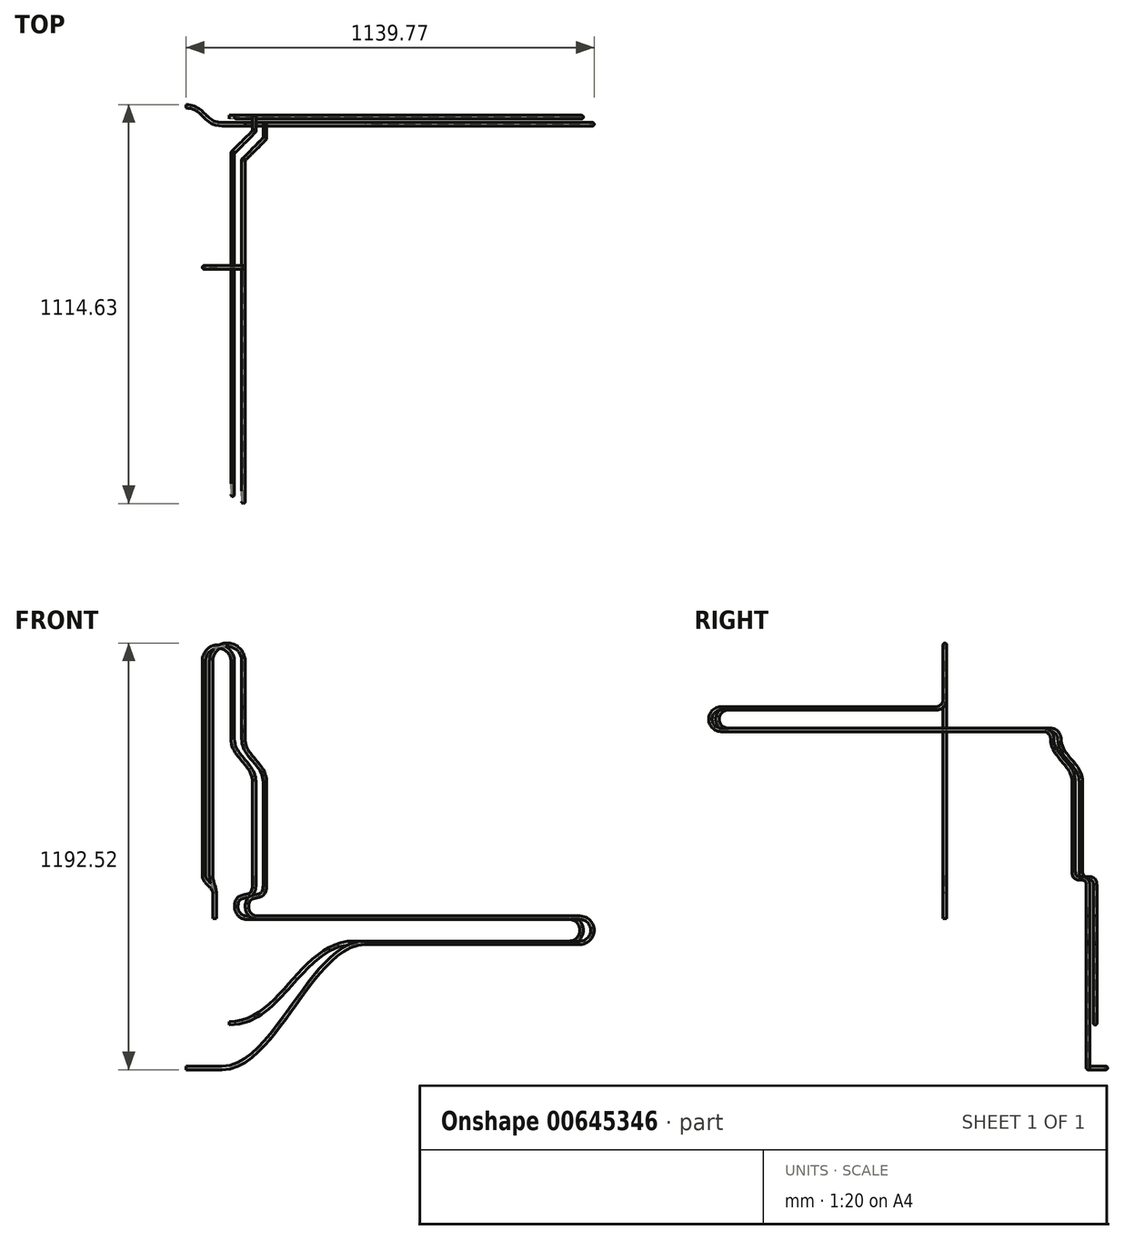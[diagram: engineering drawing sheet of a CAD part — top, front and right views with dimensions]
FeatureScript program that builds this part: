
annotation { "Feature Type Name" : "Feature", "Feature Type Description" : "" }
export const myFeature = defineFeature(function(context is Context, id is Id, definition is map)
    precondition{}
    {
        {
            var Q0;
            Q0=qCreatedBy(makeId("Top.planeOp"),FACE);
            var sketch = newSketch(context, id + "F0", { "sketchPlane" : qUnion([Q0])});
            skCircle(sketch, "E0", {"center": v(0, 0) * mm, "radius": 4.76 * mm});
            skCircle(sketch, "E1", {"center": v(0, 0) * mm, "radius": 3.17 * mm});
            skSolve(sketch);
        }
        {
            var Q0;
            Q0=qCreatedBy(makeId("Front.planeOp"),FACE);
            var sketch = newSketch(context, id + "F1", { "sketchPlane" : qUnion([Q0])});
            skLineSegment(sketch, "E2", {"start": v(80, 612) * mm, "end": v(80, 720) * mm});
            skArc(sketch, "E3", {"start": v(80, 720) * mm, "mid": v(35, 765) * mm, "end": v(-10, 720) * mm});
            skLineSegment(sketch, "E4", {"start": v(0, 70) * mm, "end": v(0, 0) * mm});
            skFitSpline(sketch, "E5", {"points": [v(0, 70) * mm, v(-5, 95) * mm, v(-10, 120) * mm], "startDerivative": vector(0, 60) * mm, "endDerivative": vector(0, 60) * mm});
            skLineSegment(sketch, "E6", {"start": v(-10, 110) * mm, "end": v(-10, 120) * mm, "construction": true});
            skLineSegment(sketch, "E7", {"start": v(0, 80) * mm, "end": v(0, 70) * mm, "construction": true});
            skLineSegment(sketch, "E8", {"start": v(0, 70) * mm, "end": v(-10, 120) * mm, "construction": true});
            skLineSegment(sketch, "E9", {"start": v(-10, 120) * mm, "end": v(-10, 720) * mm});
            skSolve(sketch);
        }
        {
            var Q0;
            Q0=qCreatedBy(makeId("Right.planeOp"),FACE);
            var Q1;
            Q1=sQuery(id+"F1.wireOp",VERTEX,"E2.start");
            cPlane(context, id + "F2", {"entities" : qUnion([Q0, Q1]), "cplaneType" : CPlaneType.PLANE_POINT, "offset" : 25 * mm, "width" : 150 * mm, "height" : 150 * mm});
        }
        {
            var Q0;
            Q0=qCreatedBy(id+"F2.planeOp",FACE);
            var sketch = newSketch(context, id + "F3", { "sketchPlane" : qUnion([Q0])});
            skArc(sketch, "E10.MirrorCS", {"start": v(0, 612) * mm, "mid": v(-7.32, 594.32) * mm, "end": v(-25, 587) * mm});
            skArc(sketch, "E11.MirrorCS", {"start": v(275, 527) * mm, "mid": v(292.68, 519.68) * mm, "end": v(300, 502) * mm});
            skLineSegment(sketch, "E12.MirrorCS", {"start": v(300, 502) * mm, "end": v(300, 517.1) * mm, "construction": true});
            skLineSegment(sketch, "E13.MirrorCS", {"start": v(-25, 587) * mm, "end": v(-625, 587) * mm});
            skArc(sketch, "E14.MirrorCS", {"start": v(-625, 527) * mm, "mid": v(-655, 557) * mm, "end": v(-625, 587) * mm});
            skLineSegment(sketch, "E15.MirrorCS", {"start": v(-625, 527) * mm, "end": v(275, 527) * mm});
            skSolve(sketch);
        }
        {
            var Q0;
            Q0=sQuery(id+"F3.wireOp",EDGE,"E12.MirrorCS");
            cPlane(context, id + "F4", {"entities" : qUnion([Q0]), "cplaneType" : CPlaneType.LINE_ANGLE, "offset" : 25 * mm, "angle" : 45 * degree, "oppositeDirection" : true, "width" : 150 * mm, "height" : 150 * mm});
        }
        {
            var Q0;
            Q0=qCreatedBy(id+"F4.planeOp",FACE);
            var sketch = newSketch(context, id + "F5", { "sketchPlane" : qUnion([Q0])});
            skFitSpline(sketch, "E16", {"points": [v(268.7, 502) * mm, v(311.2, 442) * mm, v(353.7, 382) * mm], "startDerivative": vector(0, -150) * mm, "endDerivative": vector(0, -150) * mm});
            skLineSegment(sketch, "E17", {"start": v(268.7, 477) * mm, "end": v(268.7, 502) * mm, "construction": true});
            skLineSegment(sketch, "E18", {"start": v(353.7, 407) * mm, "end": v(353.7, 382) * mm, "construction": true});
            skLineSegment(sketch, "E19", {"start": v(353.7, 382) * mm, "end": v(268.7, 502) * mm, "construction": true});
            skLineSegment(sketch, "E20", {"start": v(353.7, 382) * mm, "end": v(353.7, 132) * mm});
            skSolve(sketch);
        }
        {
            var Q0;
            Q0=qCreatedBy(makeId("Right.planeOp"),FACE);
            var Q1;
            Q1=sQuery(id+"F5.wireOp",VERTEX,"E20.end");
            cPlane(context, id + "F6", {"entities" : qUnion([Q0, Q1]), "cplaneType" : CPlaneType.PLANE_POINT, "offset" : 25 * mm, "width" : 150 * mm, "height" : 150 * mm});
        }
        {
            var Q0;
            Q0=qCreatedBy(id+"F6.planeOp",FACE);
            var sketch = newSketch(context, id + "F7", { "sketchPlane" : qUnion([Q0])});
            skFitSpline(sketch, "E21", {"points": [v(360.1, 132) * mm, v(380.1, 112) * mm, v(400.1, 92) * mm], "startDerivative": vector(0, -120) * mm, "endDerivative": vector(0, -120) * mm});
            skLineSegment(sketch, "E22", {"start": v(360.1, 132) * mm, "end": v(360.1, 112) * mm, "construction": true});
            skLineSegment(sketch, "E23", {"start": v(400.1, 112) * mm, "end": v(400.1, 92) * mm, "construction": true});
            skLineSegment(sketch, "E24", {"start": v(400.1, 92) * mm, "end": v(360.1, 132) * mm, "construction": true});
            skSolve(sketch);
        }
        {
            var Q0;
            Q0=sQuery(id+"F7.wireOp",VERTEX,"E21.end");
            var Q1;
            Q1=qCreatedBy(makeId("Front.planeOp"),FACE);
            cPlane(context, id + "F8", {"entities" : qUnion([Q0, Q1]), "cplaneType" : CPlaneType.PLANE_POINT, "offset" : 25 * mm, "width" : 150 * mm, "height" : 150 * mm});
        }
        {
            var Q0;
            Q0=qCreatedBy(id+"F8.planeOp",FACE);
            var sketch = newSketch(context, id + "F9", { "sketchPlane" : qUnion([Q0])});
            skFitSpline(sketch, "E25", {"points": [v(140.1, 92) * mm, v(115.1, 62) * mm, v(90.1, 32) * mm], "startDerivative": vector(0, -150) * mm, "endDerivative": vector(0, -150) * mm});
            skLineSegment(sketch, "E26", {"start": v(140.1, 92) * mm, "end": v(140.1, 67) * mm, "construction": true});
            skLineSegment(sketch, "E27", {"start": v(90.1, 57) * mm, "end": v(90.1, 32) * mm, "construction": true});
            skLineSegment(sketch, "E28", {"start": v(90.1, 32) * mm, "end": v(140.1, 92) * mm, "construction": true});
            skArc(sketch, "E29", {"start": v(90.1, 32) * mm, "mid": v(98.9, 10.79) * mm, "end": v(120.1, 2) * mm});
            skLineSegment(sketch, "E30", {"start": v(120.1, 2) * mm, "end": v(1020.1, 2) * mm});
            skArc(sketch, "E31", {"start": v(1020.1, -68) * mm, "mid": v(1055.1, -33) * mm, "end": v(1020.1, 2) * mm});
            skLineSegment(sketch, "E32", {"start": v(1020.1, -68) * mm, "end": v(420.1, -68) * mm});
            skFitSpline(sketch, "E33", {"points": [v(420.1, -68) * mm, v(220.1, -243) * mm, v(20.1, -418) * mm], "startDerivative": vector(-450, 0) * mm, "endDerivative": vector(-450, 0) * mm});
            skLineSegment(sketch, "E34", {"start": v(420.1, -68) * mm, "end": v(345.1, -68) * mm, "construction": true});
            skLineSegment(sketch, "E35", {"start": v(95.1, -418) * mm, "end": v(20.1, -418) * mm, "construction": true});
            skLineSegment(sketch, "E36", {"start": v(20.1, -418) * mm, "end": v(420.1, -68) * mm, "construction": true});
            skSolve(sketch);
        }
        {
            var Q0;
            Q0=sQuery(id+"F9.wireOp",VERTEX,"E33.end");
            var Q1;
            Q1=qCreatedBy(makeId("Top.planeOp"),FACE);
            cPlane(context, id + "F10", {"entities" : qUnion([Q0, Q1]), "cplaneType" : CPlaneType.PLANE_POINT, "offset" : 25 * mm, "width" : 150 * mm, "height" : 150 * mm});
        }
        {
            var Q0;
            Q0=qCreatedBy(id+"F10.planeOp",FACE);
            var sketch = newSketch(context, id + "F11", { "sketchPlane" : qUnion([Q0])});
            skFitSpline(sketch, "E37", {"points": [v(20.1, 400.1) * mm, v(-29.9, 425.1) * mm, v(-79.9, 450.1) * mm], "startDerivative": vector(-150, 0) * mm, "endDerivative": vector(-150, 0) * mm});
            skLineSegment(sketch, "E38", {"start": v(-4.9, 400.1) * mm, "end": v(20.1, 400.1) * mm, "construction": true});
            skLineSegment(sketch, "E39", {"start": v(-54.9, 450.1) * mm, "end": v(-79.9, 450.1) * mm, "construction": true});
            skLineSegment(sketch, "E40", {"start": v(-79.9, 450.1) * mm, "end": v(20.1, 400.1) * mm, "construction": true});
            skSolve(sketch);
        }
        {
            var Q0;
            Q0=qSketchRegion(id+"F0",true);
            var Q1;
            Q1=qConstructionFilter(qBodyType(qCreatedBy(id+"F1",EDGE),BodyType.WIRE),ConstructionObject.NO);
            var Q2;
            Q2=qConstructionFilter(qBodyType(qCreatedBy(id+"F3",EDGE),BodyType.WIRE),ConstructionObject.NO);
            var Q3;
            Q3=qConstructionFilter(qBodyType(qCreatedBy(id+"F5",EDGE),BodyType.WIRE),ConstructionObject.NO);
            var Q4;
            Q4=qConstructionFilter(qBodyType(qCreatedBy(id+"F7",EDGE),BodyType.WIRE),ConstructionObject.NO);
            var Q5;
            Q5=qConstructionFilter(qBodyType(qCreatedBy(id+"F9",EDGE),BodyType.WIRE),ConstructionObject.NO);
            var Q6;
            Q6=qConstructionFilter(qBodyType(qCreatedBy(id+"F11",EDGE),BodyType.WIRE),ConstructionObject.NO);
            sweep(context, id + "F12", {"profiles" : qUnion([Q0]), "path" : qUnion([Q1, Q2, Q3, Q4, Q5, Q6])});
        }
        {
            var Q0;
            Q0=qCreatedBy(makeId("Front.planeOp"),FACE);
            var sketch = newSketch(context, id + "F13", { "sketchPlane" : qUnion([Q0])});
            skLineSegment(sketch, "E41", {"start": v(50, 612) * mm, "end": v(50, 720) * mm});
            skArc(sketch, "E42", {"start": v(50, 720) * mm, "mid": v(10, 760) * mm, "end": v(-30, 720) * mm});
            skLineSegment(sketch, "E43", {"start": v(0, 70) * mm, "end": v(0, 0) * mm});
            skFitSpline(sketch, "E44", {"points": [v(0, 70) * mm, v(-15, 95) * mm, v(-30, 120) * mm], "startDerivative": vector(0, 60) * mm, "endDerivative": vector(0, 60) * mm});
            skLineSegment(sketch, "E45", {"start": v(-30, 110) * mm, "end": v(-30, 120) * mm, "construction": true});
            skLineSegment(sketch, "E46", {"start": v(0, 80) * mm, "end": v(0, 70) * mm, "construction": true});
            skLineSegment(sketch, "E47", {"start": v(0, 70) * mm, "end": v(-30, 120) * mm, "construction": true});
            skLineSegment(sketch, "E48", {"start": v(-30, 120) * mm, "end": v(-30, 720) * mm});
            skSolve(sketch);
        }
        {
            var Q0;
            Q0=qCreatedBy(makeId("Right.planeOp"),FACE);
            var Q1;
            Q1=sQuery(id+"F13.wireOp",VERTEX,"E41.start");
            cPlane(context, id + "F14", {"entities" : qUnion([Q0, Q1]), "cplaneType" : CPlaneType.PLANE_POINT, "offset" : 25 * mm, "width" : 150 * mm, "height" : 150 * mm});
        }
        {
            var Q0;
            Q0=qCreatedBy(id+"F14.planeOp",FACE);
            var sketch = newSketch(context, id + "F15", { "sketchPlane" : qUnion([Q0])});
            skArc(sketch, "E49.MirrorCS", {"start": v(0, 612) * mm, "mid": v(-7.32, 594.32) * mm, "end": v(-25, 587) * mm});
            skArc(sketch, "E50.MirrorCS", {"start": v(295, 527) * mm, "mid": v(312.68, 519.68) * mm, "end": v(320, 502) * mm});
            skLineSegment(sketch, "E51.MirrorCS", {"start": v(320, 502) * mm, "end": v(320, 517.1) * mm, "construction": true});
            skLineSegment(sketch, "E52.MirrorCS", {"start": v(-25, 587) * mm, "end": v(-605, 587) * mm});
            skArc(sketch, "E53.MirrorCS", {"start": v(-605, 527) * mm, "mid": v(-635, 557) * mm, "end": v(-605, 587) * mm});
            skLineSegment(sketch, "E54.MirrorCS", {"start": v(-605, 527) * mm, "end": v(295, 527) * mm});
            skSolve(sketch);
        }
        {
            var Q0;
            Q0=sQuery(id+"F15.wireOp",EDGE,"E51.MirrorCS");
            cPlane(context, id + "F16", {"entities" : qUnion([Q0]), "cplaneType" : CPlaneType.LINE_ANGLE, "offset" : 25 * mm, "angle" : 45 * degree, "oppositeDirection" : true, "width" : 150 * mm, "height" : 150 * mm});
        }
        {
            var Q0;
            Q0=qCreatedBy(id+"F16.planeOp",FACE);
            var sketch = newSketch(context, id + "F17", { "sketchPlane" : qUnion([Q0])});
            skFitSpline(sketch, "E55", {"points": [v(261.63, 502) * mm, v(304.13, 442) * mm, v(346.63, 382) * mm], "startDerivative": vector(0, -150) * mm, "endDerivative": vector(0, -150) * mm});
            skLineSegment(sketch, "E56", {"start": v(261.63, 477) * mm, "end": v(261.63, 502) * mm, "construction": true});
            skLineSegment(sketch, "E57", {"start": v(346.63, 407) * mm, "end": v(346.63, 382) * mm, "construction": true});
            skLineSegment(sketch, "E58", {"start": v(346.63, 382) * mm, "end": v(261.63, 502) * mm, "construction": true});
            skLineSegment(sketch, "E59", {"start": v(346.63, 382) * mm, "end": v(346.63, 132) * mm});
            skSolve(sketch);
        }
        {
            var Q0;
            Q0=qCreatedBy(makeId("Right.planeOp"),FACE);
            var Q1;
            Q1=sQuery(id+"F17.wireOp",VERTEX,"E59.end");
            cPlane(context, id + "F18", {"entities" : qUnion([Q0, Q1]), "cplaneType" : CPlaneType.PLANE_POINT, "offset" : 25 * mm, "width" : 150 * mm, "height" : 150 * mm});
        }
        {
            var Q0;
            Q0=qCreatedBy(id+"F18.planeOp",FACE);
            var sketch = newSketch(context, id + "F19", { "sketchPlane" : qUnion([Q0])});
            skFitSpline(sketch, "E60", {"points": [v(380.1, 132) * mm, v(400.1, 112) * mm, v(420.1, 92) * mm], "startDerivative": vector(0, -120) * mm, "endDerivative": vector(0, -120) * mm});
            skLineSegment(sketch, "E61", {"start": v(380.1, 132) * mm, "end": v(380.1, 112) * mm, "construction": true});
            skLineSegment(sketch, "E62", {"start": v(420.1, 112) * mm, "end": v(420.1, 92) * mm, "construction": true});
            skLineSegment(sketch, "E63", {"start": v(420.1, 92) * mm, "end": v(380.1, 132) * mm, "construction": true});
            skSolve(sketch);
        }
        {
            var Q0;
            Q0=qCreatedBy(makeId("Front.planeOp"),FACE);
            var Q1;
            Q1=sQuery(id+"F19.wireOp",VERTEX,"E60.end");
            cPlane(context, id + "F20", {"entities" : qUnion([Q0, Q1]), "cplaneType" : CPlaneType.PLANE_POINT, "offset" : 25 * mm, "width" : 150 * mm, "height" : 150 * mm});
        }
        {
            var Q0;
            Q0=qCreatedBy(id+"F20.planeOp",FACE);
            var sketch = newSketch(context, id + "F21", { "sketchPlane" : qUnion([Q0])});
            skFitSpline(sketch, "E64", {"points": [v(110.1, 92) * mm, v(85.1, 62) * mm, v(60.1, 32) * mm], "startDerivative": vector(0, -150) * mm, "endDerivative": vector(0, -150) * mm});
            skLineSegment(sketch, "E65", {"start": v(110.1, 92) * mm, "end": v(110.1, 67) * mm, "construction": true});
            skLineSegment(sketch, "E66", {"start": v(60.1, 57) * mm, "end": v(60.1, 32) * mm, "construction": true});
            skLineSegment(sketch, "E67", {"start": v(60.1, 32) * mm, "end": v(110.1, 92) * mm, "construction": true});
            skArc(sketch, "E68", {"start": v(60.1, 32) * mm, "mid": v(68.9, 10.79) * mm, "end": v(90.1, 2) * mm});
            skLineSegment(sketch, "E69", {"start": v(90.1, 2) * mm, "end": v(990.1, 2) * mm});
            skArc(sketch, "E70", {"start": v(990.1, -68) * mm, "mid": v(1025.1, -33) * mm, "end": v(990.1, 2) * mm});
            skLineSegment(sketch, "E71", {"start": v(990.1, -68) * mm, "end": v(390.1, -68) * mm});
            skFitSpline(sketch, "E72", {"points": [v(390.1, -68) * mm, v(215.1, -180.5) * mm, v(40.1, -293) * mm], "startDerivative": vector(-450, 0) * mm, "endDerivative": vector(-450, 0) * mm});
            skLineSegment(sketch, "E73", {"start": v(390.1, -68) * mm, "end": v(315.1, -68) * mm, "construction": true});
            skLineSegment(sketch, "E74", {"start": v(115.1, -293) * mm, "end": v(40.1, -293) * mm, "construction": true});
            skLineSegment(sketch, "E75", {"start": v(40.1, -293) * mm, "end": v(390.1, -68) * mm, "construction": true});
            skSolve(sketch);
        }
        {
            var Q0;
            Q0=qSketchRegion(id+"F0",true);
            var Q1;
            Q1=qConstructionFilter(qBodyType(qCreatedBy(id+"F13",EDGE),BodyType.WIRE),ConstructionObject.NO);
            var Q2;
            Q2=qConstructionFilter(qBodyType(qCreatedBy(id+"F15",EDGE),BodyType.WIRE),ConstructionObject.NO);
            var Q3;
            Q3=qConstructionFilter(qBodyType(qCreatedBy(id+"F17",EDGE),BodyType.WIRE),ConstructionObject.NO);
            var Q4;
            Q4=qConstructionFilter(qBodyType(qCreatedBy(id+"F19",EDGE),BodyType.WIRE),ConstructionObject.NO);
            var Q5;
            Q5=qConstructionFilter(qBodyType(qCreatedBy(id+"F21",EDGE),BodyType.WIRE),ConstructionObject.NO);
            sweep(context, id + "F22", {"profiles" : qUnion([Q0]), "path" : qUnion([Q1, Q2, Q3, Q4, Q5])});
        }
    });
